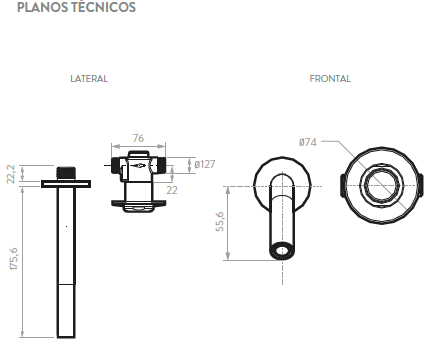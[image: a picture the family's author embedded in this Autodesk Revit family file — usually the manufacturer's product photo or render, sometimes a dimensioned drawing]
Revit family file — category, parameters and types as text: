
# Revit family: FT 701310001_Lavamanos Pico Expuesto Push
name_source: partatom
category: Plumbing Fixtures
units: mm (PartAtom-declared; Revit-internal decimal feet)

## family parameters
Always vertical = Yes
Cut with Voids When Loaded = No
Host = Wall
OmniClass Number = 23.31.11.00
OmniClass Title = Faucets
Part Type = Normal
Room Calculation Point = No
Round Connector Dimension = Use Diameter
Shared = No

## types (1)
- PUSH
    Alto = 900 mm  [stored 2.95276 ft]
    Ciclo de Vida y Desempeño de la descarga = 150,000 ciclos.
    Creado por = IDD
    Description = Las grifierías de lavamanos Corona son el aliado perfecto para las necesidades
de las instituciones de alto tráfico, están diseñadas para un óptimo
funcioamiento y durabilidad debido a sus características antivandálicas • Grifiería de Lavamanos antivandálica con regadera de pico expuesto.
• Consumo de agua desde 0.41 L hasta 1.9 L de acuerdo al cartucho.
• Cierre automático temporizado entre 5 a 9 segundos.
    Fecha de creación = 2/07/2020
    Flujo max @80psi = 9,68 L/min - 0,49 L/Descarga
    Flujo reaL (L/min) = 6,5 - 9,68 L/min - 0,33 - 0,49 L/Descarga
    Garantía = 3 años
    Garantía Acabados = 2 años
    Manufacturer = Corona
    Material = Corona_Cromado
    Material Conector = Corona_Cobre
    Model = Grifería para Lavamanos Institucional de Empotrar Push Pico Expuesto
    Peso Bruto aprox = 860gr. / 1,90Lb.
    Peso Neto aprox = 77gr. / 1,70Lb
    Presión máxima recomendada = 80 psi elástica
    Presión mínima recomendada = 20 psi elástica.
    Torque de cierre = Ajustar con una llave hasta obtener un selle perfecto
    URL = https://corona.co

note: [stored X ft] marks values corroborated as IEEE doubles in the binary element streams (Revit-internal decimal feet)

## geometry (parser evidence)
native form markers: Sweep x7
no freeform markers — native parametric forms only
